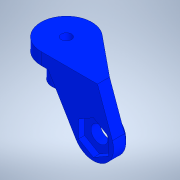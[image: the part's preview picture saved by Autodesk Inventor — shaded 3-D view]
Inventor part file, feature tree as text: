
AUTODESK INVENTOR PART (.ipt)
format: ipt  version: 2020 (Build 240168000, 168)  size: 207,360 bytes
history: native  units: mm
features: extrude x6, sketch x6, chamfer x3, projected_geometry x1
ambient origin geometry x8: Origin, YZ Plane, XZ Plane, XY Plane, X Axis, Y Axis, Z Axis, Center Point
bodies: Solid1 (feature_tree)
feature tree (16):
  extrude  "Extrusion1"  Depth=10.0mm
  extrude  "Extrusion2"  TaperAngle=0.0deg  [1 undecoded]
  extrude  "Extrusion3"  Depth=7.4mm
  chamfer  "Chamfer1"  Distance=1.5mm
  extrude  "Extrusion6"  Depth=0.8mm TaperAngle=0.0deg
  extrude  "Extrusion7"  Depth=2.0mm
  chamfer  "Chamfer2"  Distance=2.5mm
  extrude  "Extrusion8"  Depth=2.5mm
  chamfer  "Chamfer3"  Distance=3.0mm
  sketch  "Sketch1"  dims[d0=10.0mm d1=4.2mm]
  sketch  "Sketch2"  dims[d2=12.0mm d4=0.0mm]
  sketch  "Sketch4"  dims[d5=3.0mm d6=0.0mm d7=7.4mm d8=1.5mm d9=0.0mm]
  sketch  "Sketch6"  dims[d10=8.5mm d11=0.8mm d12=0.0mm]
  projected_geometry  "Projected Loop1"
  sketch  "Sketch7"  dims[d13=0.8mm d14=2.0mm d15=45.0deg d25=14.0mm]
  sketch  "Sketch8"  dims[d26=6.0mm d27=2.5mm d28=2.5mm d29=3.0mm d30=0.0mm d31=7.0mm d32=6.0mm d33=0.0mm d34=2.0mm d35=2.0mm d36=45.0deg d37=2.0mm d38=0.0mm d39=2.0mm d40=2.0mm d41=45.0deg]
note: 1 required parameter value undecoded (feature->parameter linkage not recoverable at this tier; creation-order binding heuristic only, values carry confidence <= 0.55)
